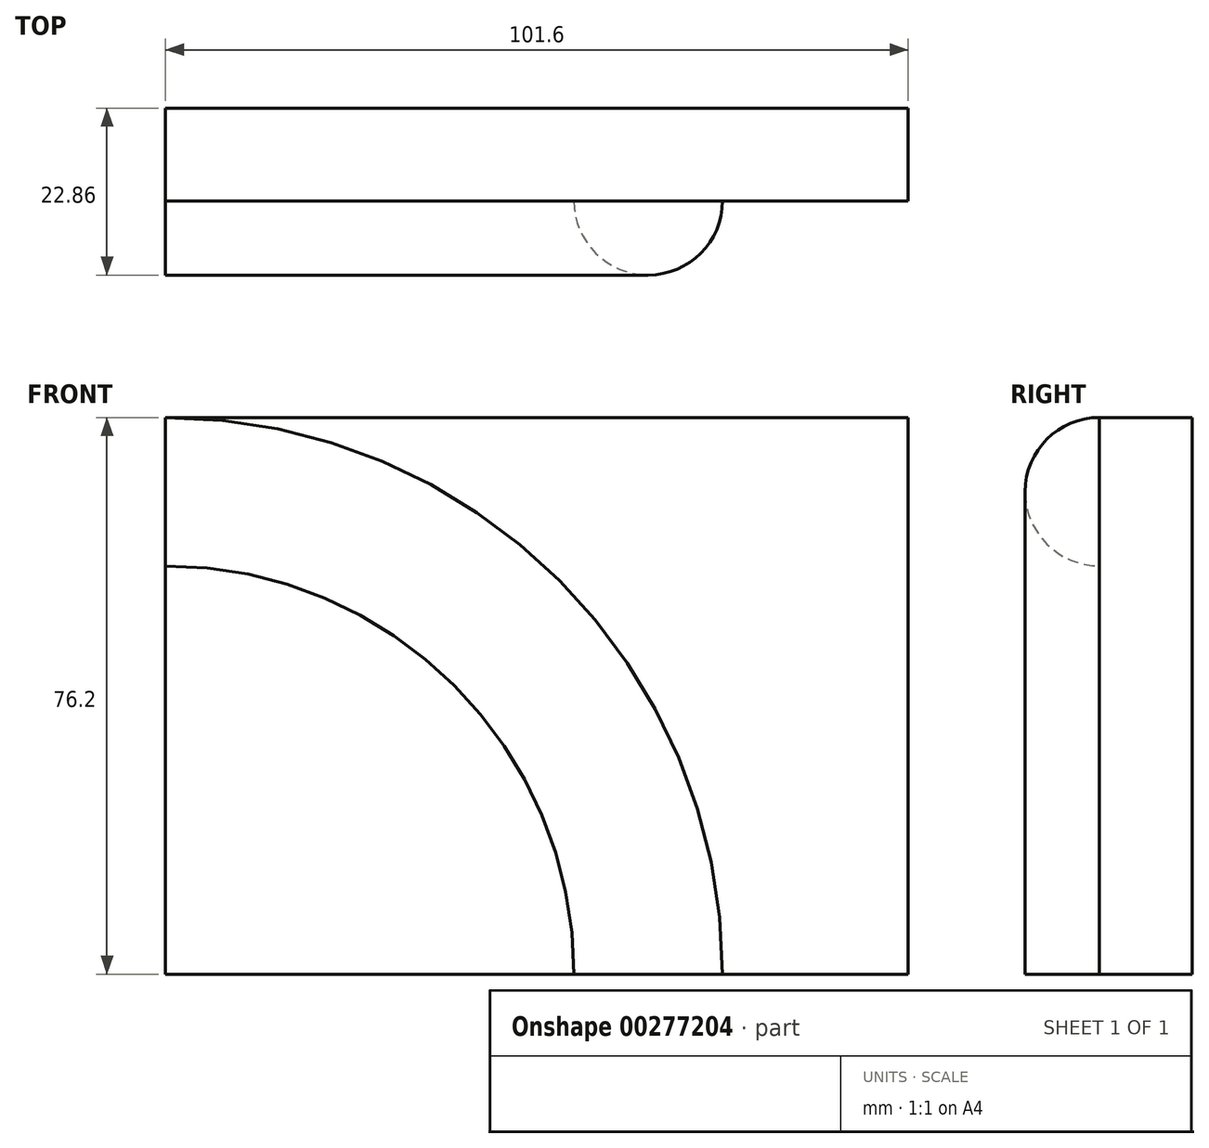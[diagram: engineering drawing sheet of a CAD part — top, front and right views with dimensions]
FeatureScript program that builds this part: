
annotation { "Feature Type Name" : "Feature", "Feature Type Description" : "" }
export const myFeature = defineFeature(function(context is Context, id is Id, definition is map)
    precondition{}
    {
        {
            var Q0;
            Q0=qCreatedBy(makeId("Front.planeOp"),FACE);
            var sketch = newSketch(context, id + "F0", { "sketchPlane" : qUnion([Q0])});
            skLineSegment(sketch, "E0.bottom", {"start": v(0, 0) * mm, "end": v(101.6, 0) * mm});
            skLineSegment(sketch, "E0.top", {"start": v(0, 76.2) * mm, "end": v(101.6, 76.2) * mm});
            skLineSegment(sketch, "E0.left", {"start": v(0, 0) * mm, "end": v(0, 76.2) * mm});
            skLineSegment(sketch, "E0.right", {"start": v(101.6, 0) * mm, "end": v(101.6, 76.2) * mm});
            skArc(sketch, "E1", {"start": v(0, 76.2) * mm, "mid": v(53.88, 53.88) * mm, "end": v(76.2, 0) * mm});
            skSolve(sketch);
        }
        {
            var Q0;
            Q0=makeQuery(id+"F0.imprint","IMPRINT",FACE,{"disambiguationData":[TD([[makeQuery(id+"F0.imprint","IMPRINT",EDGE,{"derivedFrom":sQuery(id+"F0.wireOp",EDGE,"E0.bottom")}),1.0]])]});
            var Q1;
            Q1=makeQuery(id+"F0.imprint","IMPRINT",FACE,{"disambiguationData":[TD([[makeQuery(id+"F0.imprint","IMPRINT",EDGE,{"derivedFrom":sQuery(id+"F0.wireOp",EDGE,"E0.top")}),-1.0]])]});
            extrude(context, id + "F1", {"entities" : qUnion([Q0, Q1]), "oppositeDirection" : true, "depth" : 12.7 * mm});
        }
        {
            var Q0;
            Q0=qCreatedBy(makeId("Right.planeOp"),FACE);
            var sketch = newSketch(context, id + "F2", { "sketchPlane" : qUnion([Q0])});
            skLineSegment(sketch, "E2", {"start": v(0, 0) * mm, "end": v(0, 76.2) * mm});
            skArc(sketch, "E3", {"start": v(0, 76.2) * mm, "mid": v(-10.16, 66.04) * mm, "end": v(0, 55.88) * mm});
            skSolve(sketch);
        }
        {
            var Q0;
            {var subQ0=sQuery(id+"F2.wireOp",EDGE,"E3");Q0=makeQuery(id+"F2.imprint","IMPRINT",FACE,{"disambiguationData":[TD([[makeQuery(id+"F2.imprint","IMPRINT",EDGE,{"derivedFrom":subQ0}),1.0]])]});}
            var Q1;
            Q1=sQuery(id+"F0.wireOp",EDGE,"E1");
            sweep(context, id + "F3", {"profiles" : qUnion([Q0]), "path" : qUnion([Q1])});
        }
    });
